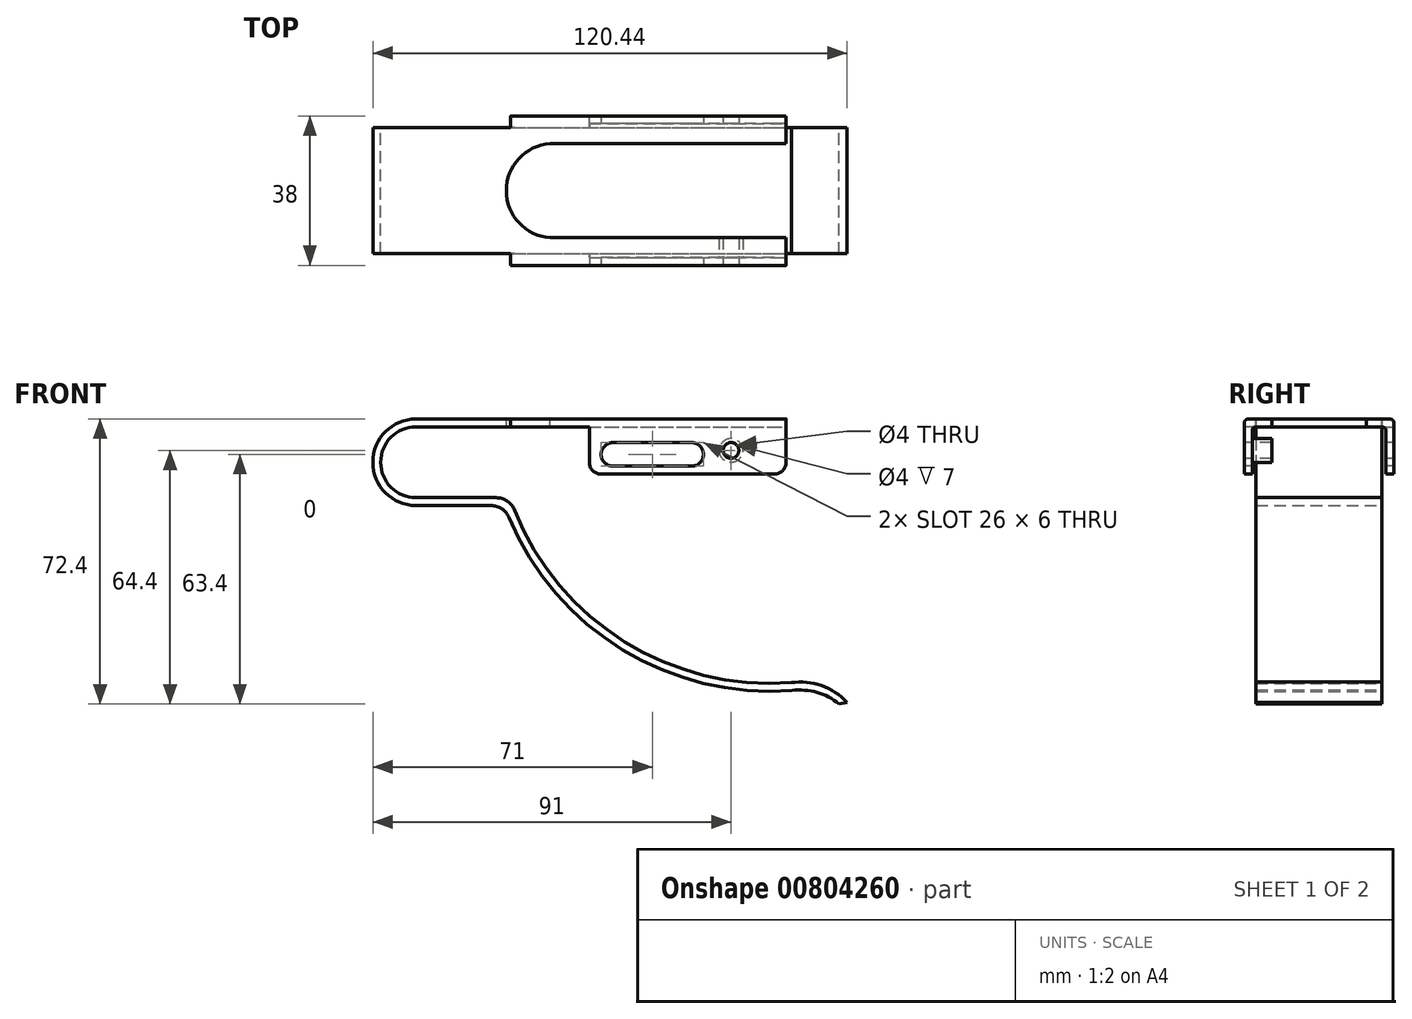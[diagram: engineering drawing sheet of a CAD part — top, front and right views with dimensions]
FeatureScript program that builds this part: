
annotation { "Feature Type Name" : "Feature", "Feature Type Description" : "" }
export const myFeature = defineFeature(function(context is Context, id is Id, definition is map)
    precondition{}
    {
        {
            var Q0;
            Q0=qCreatedBy(makeId("Front.planeOp"),FACE);
            var sketch = newSketch(context, id + "F0", { "sketchPlane" : qUnion([Q0])});
            skArc(sketch, "E0", {"start": v(0, 9) * mm, "mid": v(-9, 0) * mm, "end": v(0, -9) * mm});
            skLineSegment(sketch, "E1", {"start": v(0, 9) * mm, "end": v(94, 9) * mm});
            skLineSegment(sketch, "E2", {"start": v(0, -9) * mm, "end": v(20.34, -9) * mm});
            skArc(sketch, "E3", {"start": v(24.99, -12.15) * mm, "mid": v(52.96, -45.6) * mm, "end": v(95.3, -56) * mm});
            skArc(sketch, "E4", {"start": v(109.44, -61) * mm, "mid": v(103, -56.74) * mm, "end": v(95.3, -56) * mm});
            skPoint(sketch, "E5.visualSharp", {"position": v(23.82, -9) * mm});
            skArc(sketch, "E5.filletArc", {"start": v(24.99, -12.15) * mm, "mid": v(23.15, -9.86) * mm, "end": v(20.34, -9) * mm});
            skLineSegment(sketch, "E6.1", {"start": v(0, 11) * mm, "end": v(94, 11) * mm});
            skArc(sketch, "E6.2", {"start": v(0, 11) * mm, "mid": v(-11, 0) * mm, "end": v(0, -11) * mm});
            skLineSegment(sketch, "E6.3", {"start": v(0, -11) * mm, "end": v(19, -11) * mm});
            skLineSegment(sketch, "E7", {"start": v(94, 11) * mm, "end": v(94, 9) * mm});
            skPoint(sketch, "E8.visualSharp", {"position": v(22.4, -11) * mm});
            skArc(sketch, "E8.filletArc", {"start": v(23.61, -14.06) * mm, "mid": v(21.77, -11.84) * mm, "end": v(19, -11) * mm});
            skArc(sketch, "E9", {"start": v(107.48, -61.4) * mm, "mid": v(101.83, -58.48) * mm, "end": v(95.48, -58) * mm});
            skArc(sketch, "E10.0", {"start": v(23.61, -14.06) * mm, "mid": v(52.45, -47.64) * mm, "end": v(95.48, -58) * mm});
            skLineSegment(sketch, "E11", {"start": v(107.48, -61.4) * mm, "end": v(109.44, -61) * mm});
            skSolve(sketch);
        }
        {
            var Q0;
            Q0 = qSketchRegion(id + "F0", true);
            extrude(context, id + "F1", {"entities" : qUnion([Q0]), "depth" : 16 * mm, "offsetDistance" : 25 * mm});
        }
        {
            var Q0;
            Q0=makeQuery(id+"F1.opExtrude","SWEPT_FACE",FACE,{"disambiguationData":[OSD([sQuery(id+"F0.wireOp",EDGE,"E6.1")])]});
            var sketch = newSketch(context, id + "F2", { "sketchPlane" : qUnion([Q0])});
            skSolve(sketch);
        }
        {
            var Q0;
            {var subQ0=sQuery(id+"F0.wireOp",EDGE,"E6.1");Q0=makeQuery(id+"F2.imprint","IMPRINT",FACE,{"disambiguationData":[TD([[makeQuery(id+"F2.imprint","IMPRINT",EDGE,{"derivedFrom":makeQuery(id+"F1.opExtrude","CAP_EDGE",EDGE,{"disambiguationData":[OSD([subQ0])],"isStart":true})}),-1.0]])]});}
            var sketch = newSketch(context, id + "F3", { "sketchPlane" : qUnion([Q0])});
            skLineSegment(sketch, "E12.bottom", {"start": v(94, -16) * mm, "end": v(24, -16) * mm});
            skLineSegment(sketch, "E12.top", {"start": v(94, -19) * mm, "end": v(24, -19) * mm});
            skLineSegment(sketch, "E12.left", {"start": v(94, -16) * mm, "end": v(94, -19) * mm});
            skLineSegment(sketch, "E12.right", {"start": v(24, -16) * mm, "end": v(24, -19) * mm});
            skSolve(sketch);
        }
        {
            var Q0;
            Q0 = qSketchRegion(id + "F3", true);
            extrude(context, id + "F4", {"entities" : qUnion([Q0]), "operationType" : NewBodyOperationType.ADD, "oppositeDirection" : true, "depth" : 2 * mm, "offsetDistance" : 25 * mm});
        }
        {
            var Q0;
            Q0=makeQuery(id+"F4.opExtrude","SWEPT_FACE",FACE,{"disambiguationData":[OSD([sQuery(id+"F3.wireOp",EDGE,"E12.top")])]});
            var sketch = newSketch(context, id + "F5", { "sketchPlane" : qUnion([Q0])});
            skLineSegment(sketch, "E13.bottom", {"start": v(94, 11) * mm, "end": v(44, 11) * mm});
            skLineSegment(sketch, "E13.top", {"start": v(94, -3) * mm, "end": v(44, -3) * mm});
            skLineSegment(sketch, "E13.left", {"start": v(94, 11) * mm, "end": v(94, -3) * mm});
            skLineSegment(sketch, "E13.right", {"start": v(44, 11) * mm, "end": v(44, -3) * mm});
            skSolve(sketch);
        }
        {
            var Q0;
            Q0 = qSketchRegion(id + "F5", true);
            extrude(context, id + "F6", {"entities" : qUnion([Q0]), "operationType" : NewBodyOperationType.ADD, "oppositeDirection" : true, "depth" : 2 * mm, "offsetDistance" : 25 * mm});
        }
        {
            var Q0;
            Q0=makeQuery(id+"F4.opExtrude","CAP_EDGE",EDGE,{"disambiguationData":[OSD([sQuery(id+"F3.wireOp",EDGE,"E12.top")])],"isStart":true});
            var Q1;
            Q1=makeQuery(id+"F6.boolean.opBoolean","INTERSECT",EDGE,{"derivedFrom":[makeQuery(id+"F4.boolean.opBoolean","MERGE",FACE,{"derivedFrom":[makeQuery(id+"F1.opExtrude","SWEPT_FACE",FACE,{"disambiguationData":[OSD([sQuery(id+"F0.wireOp",EDGE,"E1")])]}),makeQuery(id+"F4.opExtrude","CAP_FACE",FACE,{"disambiguationData":[OSD([sQuery(id+"F3.wireOp",EDGE,"E12.bottom"),sQuery(id+"F3.wireOp",EDGE,"E12.top"),sQuery(id+"F3.wireOp",EDGE,"E12.left"),sQuery(id+"F3.wireOp",EDGE,"E12.right")])],"isStart":false})]}),makeQuery(id+"F6.opExtrude","CAP_FACE",FACE,{"disambiguationData":[OSD([sQuery(id+"F5.wireOp",EDGE,"E13.bottom"),sQuery(id+"F5.wireOp",EDGE,"E13.top"),sQuery(id+"F5.wireOp",EDGE,"E13.left"),sQuery(id+"F5.wireOp",EDGE,"E13.right")])],"isStart":false})]});
            fillet(context, id + "F7", {"entities" : qUnion([Q0, Q1]), "radius" : 1 * mm, "tangentPropagation" : true, "allowEdgeOverflow" : false});
        }
        {
            var Q0;
            Q0=makeQuery(id+"F1.opExtrude","SWEPT_BODY",BODY,{"disambiguationData":[OSD([sQuery(id+"F0.wireOp",EDGE,"E0"),sQuery(id+"F0.wireOp",EDGE,"E1"),sQuery(id+"F0.wireOp",EDGE,"E2"),sQuery(id+"F0.wireOp",EDGE,"E3"),sQuery(id+"F0.wireOp",EDGE,"E4"),sQuery(id+"F0.wireOp",EDGE,"E5.filletArc"),sQuery(id+"F0.wireOp",EDGE,"E6.1"),sQuery(id+"F0.wireOp",EDGE,"E6.2"),sQuery(id+"F0.wireOp",EDGE,"E6.3"),sQuery(id+"F0.wireOp",EDGE,"E7"),sQuery(id+"F0.wireOp",EDGE,"E8.filletArc"),sQuery(id+"F0.wireOp",EDGE,"E9"),sQuery(id+"F0.wireOp",EDGE,"E10.0"),sQuery(id+"F0.wireOp",EDGE,"E11")])]});
            var Q1;
            Q1=qCreatedBy(makeId("Front.planeOp"),FACE);
            mirror(context, id + "F8", {"operationType" : NewBodyOperationType.ADD, "entities" : qUnion([Q0]), "mirrorPlane" : qUnion([Q1])});
        }
        {
            var Q0;
            {var subQ0=sQuery(id+"F0.wireOp",EDGE,"E6.1");Q0=makeQuery(id+"F2.imprint","IMPRINT",FACE,{"disambiguationData":[TD([[makeQuery(id+"F2.imprint","IMPRINT",EDGE,{"derivedFrom":makeQuery(id+"F1.opExtrude","CAP_EDGE",EDGE,{"disambiguationData":[OSD([subQ0])],"isStart":true})}),-1.0]])]});}
            var sketch = newSketch(context, id + "F9", { "sketchPlane" : qUnion([Q0])});
            skArc(sketch, "E14", {"start": v(34, 11.96) * mm, "mid": v(22.92, 0) * mm, "end": v(34, -11.96) * mm});
            skLineSegment(sketch, "E15", {"start": v(34, 11.96) * mm, "end": v(94, 11.96) * mm});
            skLineSegment(sketch, "E16", {"start": v(34, -11.96) * mm, "end": v(94, -11.96) * mm});
            skLineSegment(sketch, "E17", {"start": v(94, -11.96) * mm, "end": v(94, 11.96) * mm});
            skSolve(sketch);
        }
        {
            var Q0;
            Q0 = qSketchRegion(id + "F9", true);
            extrude(context, id + "F10", {"entities" : qUnion([Q0]), "operationType" : NewBodyOperationType.REMOVE, "oppositeDirection" : true, "depth" : 2 * mm, "offsetDistance" : 25 * mm});
        }
        {
            var Q0;
            Q0=makeQuery(id+"F6.boolean.opBoolean","MERGE",FACE,{"derivedFrom":[makeQuery(id+"F4.opExtrude","SWEPT_FACE",FACE,{"disambiguationData":[OSD([sQuery(id+"F3.wireOp",EDGE,"E12.top")])]}),makeQuery(id+"F6.opExtrude","CAP_FACE",FACE,{"disambiguationData":[OSD([sQuery(id+"F5.wireOp",EDGE,"E13.bottom"),sQuery(id+"F5.wireOp",EDGE,"E13.top"),sQuery(id+"F5.wireOp",EDGE,"E13.left"),sQuery(id+"F5.wireOp",EDGE,"E13.right")])],"isStart":true})]});
            var sketch = newSketch(context, id + "F11", { "sketchPlane" : qUnion([Q0])});
            skLineSegment(sketch, "E18", {"start": v(50, 2) * mm, "end": v(70, 2) * mm});
            skArc(sketch, "E19.0.startCap", {"start": v(50, -1) * mm, "mid": v(47, 2) * mm, "end": v(50, 5) * mm});
            skArc(sketch, "E19.0.endCap", {"start": v(70, 5) * mm, "mid": v(73, 2) * mm, "end": v(70, -1) * mm});
            skLineSegment(sketch, "E19.0.left", {"start": v(50, 5) * mm, "end": v(70, 5) * mm});
            skLineSegment(sketch, "E19.0.right", {"start": v(50, -1) * mm, "end": v(70, -1) * mm});
            skSolve(sketch);
        }
        {
            var Q0;
            Q0 = qSketchRegion(id + "F11", true);
            extrude(context, id + "F12", {"entities" : qUnion([Q0]), "operationType" : NewBodyOperationType.REMOVE, "endBound" : BoundingType.THROUGH_ALL, "oppositeDirection" : true, "depth" : 25 * mm, "offsetDistance" : 25 * mm});
        }
        {
            var Q0;
            Q0=makeQuery(id+"F6.boolean.opBoolean","MERGE",FACE,{"derivedFrom":[makeQuery(id+"F4.opExtrude","SWEPT_FACE",FACE,{"disambiguationData":[OSD([sQuery(id+"F3.wireOp",EDGE,"E12.top")])]}),makeQuery(id+"F6.opExtrude","CAP_FACE",FACE,{"disambiguationData":[OSD([sQuery(id+"F5.wireOp",EDGE,"E13.bottom"),sQuery(id+"F5.wireOp",EDGE,"E13.top"),sQuery(id+"F5.wireOp",EDGE,"E13.left"),sQuery(id+"F5.wireOp",EDGE,"E13.right")])],"isStart":true})]});
            var sketch = newSketch(context, id + "F13", { "sketchPlane" : qUnion([Q0])});
            skPoint(sketch, "E20", {"position": v(80, 3) * mm});
            skSolve(sketch);
        }
        {
            var Q0;
            Q0=sQuery(id+"F13.wireOp",VERTEX,"E20");
            var Q1;
            Q1=makeQuery(id+"F1.opExtrude","SWEPT_BODY",BODY,{"disambiguationData":[OSD([sQuery(id+"F0.wireOp",EDGE,"E0"),sQuery(id+"F0.wireOp",EDGE,"E1"),sQuery(id+"F0.wireOp",EDGE,"E2"),sQuery(id+"F0.wireOp",EDGE,"E3"),sQuery(id+"F0.wireOp",EDGE,"E4"),sQuery(id+"F0.wireOp",EDGE,"E5.filletArc"),sQuery(id+"F0.wireOp",EDGE,"E6.1"),sQuery(id+"F0.wireOp",EDGE,"E6.2"),sQuery(id+"F0.wireOp",EDGE,"E6.3"),sQuery(id+"F0.wireOp",EDGE,"E7"),sQuery(id+"F0.wireOp",EDGE,"E8.filletArc"),sQuery(id+"F0.wireOp",EDGE,"E9"),sQuery(id+"F0.wireOp",EDGE,"E10.0"),sQuery(id+"F0.wireOp",EDGE,"E11")])]});
            hole(context, id + "F14", {"style" : HoleStyle.SIMPLE, "endStyle" : HoleEndStyle.THROUGH, "holeDiameter" : 4 * mm, "majorDiameter" : 5 * mm, "isTappedThrough" : true, "tappedDepth" : 12 * mm, "tapClearance" : 3, "locations" : qUnion([Q0]), "scope" : qUnion([Q1])});
        }
        {
            var Q0;
            Q0=makeQuery(id+"F6.opExtrude","CAP_FACE",FACE,{"disambiguationData":[OSD([sQuery(id+"F5.wireOp",EDGE,"E13.bottom"),sQuery(id+"F5.wireOp",EDGE,"E13.top"),sQuery(id+"F5.wireOp",EDGE,"E13.left"),sQuery(id+"F5.wireOp",EDGE,"E13.right")])],"isStart":false});
            var sketch = newSketch(context, id + "F15", { "sketchPlane" : qUnion([Q0])});
            skCircle(sketch, "E21.0", {"center": v(-80, 3) * mm, "radius": 3 * mm});
            skSolve(sketch);
        }
        {
            var Q0;
            Q0=makeQuery(id+"F15.imprint","IMPRINT",FACE,{"disambiguationData":[TD([[makeQuery(id+"F15.imprint","IMPRINT",EDGE,{"derivedFrom":sQuery(id+"F15.wireOp",EDGE,"E21.0")}),1.0]])]});
            extrude(context, id + "F16", {"entities" : qUnion([Q0]), "operationType" : NewBodyOperationType.ADD, "depth" : 5 * mm, "offsetDistance" : 25 * mm});
        }
        {
            var Q0;
            Q0=makeQuery(id+"F6.opExtrude","SWEPT_EDGE",EDGE,{"disambiguationData":[OSD([sQuery(id+"F5.wireOp",EDGE,"E13.top"),sQuery(id+"F5.wireOp",EDGE,"E13.right")])]});
            var Q1;
            Q1=makeQuery(id+"F8.opPattern","COPY",EDGE,{"derivedFrom":makeQuery(id+"F6.opExtrude","SWEPT_EDGE",EDGE,{"disambiguationData":[OSD([sQuery(id+"F5.wireOp",EDGE,"E13.top"),sQuery(id+"F5.wireOp",EDGE,"E13.left")])]}),"instanceName":"1"});
            var Q2;
            Q2=makeQuery(id+"F6.opExtrude","SWEPT_EDGE",EDGE,{"disambiguationData":[OSD([sQuery(id+"F5.wireOp",EDGE,"E13.top"),sQuery(id+"F5.wireOp",EDGE,"E13.left")])]});
            var Q3;
            Q3=makeQuery(id+"F8.opPattern","COPY",EDGE,{"derivedFrom":makeQuery(id+"F6.opExtrude","SWEPT_EDGE",EDGE,{"disambiguationData":[OSD([sQuery(id+"F5.wireOp",EDGE,"E13.top"),sQuery(id+"F5.wireOp",EDGE,"E13.right")])]}),"instanceName":"1"});
            fillet(context, id + "F17", {"entities" : qUnion([Q0, Q1, Q2, Q3]), "radius" : 3 * mm, "tangentPropagation" : true, "allowEdgeOverflow" : false});
        }
    });
